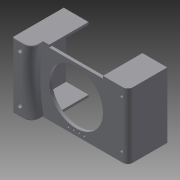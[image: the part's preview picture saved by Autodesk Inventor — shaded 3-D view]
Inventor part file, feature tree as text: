
AUTODESK INVENTOR PART (.ipt)
format: ipt  version: 2013 (Build 170138000, 138)  size: 300,032 bytes
history: native  units: in
note: dims shown in document units (in); Inventor stores cm internally (conversion verified against a paired STEP export)
features: extrude x8, sketch x7, reference x5, fillet x4, chamfer x1, projected_geometry x1
ambient origin geometry x8: Origin, YZ Plane, XZ Plane, XY Plane, X Axis, Y Axis, Z Axis, Center Point
bodies: Solid1 (feature_tree)
feature tree (26):
  extrude  "Extrusion1"  Depth=1.4961in TaperAngle=0.0deg
  extrude  "Extrusion2"  Depth=0.0394in TaperAngle=45.0deg
  extrude  "Extrusion3"  Depth=2.2047in
  chamfer  "Chamfer1"  Distance=3.937in
  extrude  "Extrusion4"  TaperAngle=0.0deg  [1 undecoded]
  fillet  "Fillet2"  Radius=0.1181in
  fillet  "Fillet3"  Radius=0.1181in
  extrude  "Extrusion5"  Depth=0.1575in
  extrude  "Extrusion6"  Depth=2.25in
  extrude  "Extrusion7"  Depth=0.15in
  fillet  "Fillet4"  Radius=0.0984in
  fillet  "Fillet6"  Radius=0.0984in
  extrude  "Extrusion8"  Depth=0.0984in
  sketch  "Sketch2"  dims[d6=0.1181in d7=0.0in d9=1.4961in d10=0.0in]
  sketch  "Sketch4"  dims[d12=0.1181in d13=0.0in d15=0.0394in d16=0.0787in d17=45.0deg]
  reference  "Reference2"
  reference  "Reference3"
  reference  "Reference4"
  reference  "Reference5"
  sketch  "Sketch5"  dims[d28=2.2047in d29=2.2047in d31=3.937in d32=0.0in]
  projected_geometry  "Projected Loop1"
  reference  "Reference14"
  sketch  "Sketch6"  dims[d41=0.2756in d42=0.0in d43=0.1181in d44=0.1181in]
  sketch  "Sketch7"  dims[d45=0.1575in d46=0.1575in]
  sketch  "Sketch8"  dims[d47=2.25in d48=2.25in]
  sketch  "Sketch9"  dims[d49=4.0in d50=0.15in d51=0.0984in d52=0.0984in d53=0.0984in d54=0.0984in d56=2.6772in d59=2.2047in d60=0.1969in d61=0.1969in d62=0.0984in d63=0.0in d64=0.0787in d66=0.1181in d67=0.0394in d68=0.0394in d69=0.1575in d78=0.6496in d79=0.2854in d80=0.2854in d81=0.1181in d82=0.0in d83=6.6929in d84=0.7874in d85=0.4724in d86=0.0in d87=0.315in d89=2.6772in d90=0.0in d91=0.0394in d92=0.1969in d93=0.0in d94=0.1969in d96=0.1969in d97=0.1575in d98=0.0in]
note: 1 required parameter value undecoded (feature->parameter linkage not recoverable at this tier; creation-order binding heuristic only, values carry confidence <= 0.55)
